# Revit family: Haworth_Riverbend_StraightBench_AP_PRELIMINARY
name_source: partatom
category: Furniture
revit_build: Autodesk Revit 2018 (Build: 20170223_1515(x64)
units: mm (PartAtom-declared; Revit-internal decimal feet)

## family parameters
Always vertical = Yes
Cut with Voids When Loaded = No
OmniClass Number = 23.40.70.14.64.21
OmniClass Title = Systems Furniture
Room Calculation Point = No
Shared = No
Work Plane-Based = No

## types (4) — shared parameters
Actual Depth = 795 mm  [stored 2.60827 ft]
Assembly Code = E2020200
Custom Size = No
Custom Width = No
Depth = 795 mm  [stored 2.60827 ft]
Description = Haworth - Riverbend - Straight Bench
Front Finish = Haworth _ Plastic _ Black
Hardware Finish = Haworth _ Paint _ Plaster
Manufacturer = Haworth
Max. Depth = 850 mm  [stored 2.78871 ft]
Max. Width = 2000 mm  [stored 6.56168 ft]
Min. Depth = 795 mm  [stored 2.60827 ft]
Min. Width = 700 mm  [stored 2.29659 ft]
Model = SERISXNX
Revision Number = 1
Size = Verify Final Dim. w/ Haworth
Trim Finish = Haworth _ Paint _ Plaster
URL = https://www.haworth.com
URL - Product = https://www.haworth.com
Warranty = http://www.haworth.com

## per-type parameters (varying)
| type | Actual Height | Actual Width | High | High Back | Low | Mid Back | No Back | Width |
| 700w x 795d x 720h - Mid Back | 390 mm  [stored 1.27953 ft] | 700 mm  [stored 2.29659 ft] | No | No | Yes | Yes | No | 700 mm  [stored 2.29659 ft] |
| 1400w x 795d x 720h - High Back | 390 mm  [stored 1.27953 ft] | 1400 mm  [stored 4.59318 ft] | No | Yes | Yes | No | No | 1400 mm  [stored 4.59318 ft] |
| 1700w x 795d x 720h - No Back | 390 mm  [stored 1.27953 ft] | 1700 mm  [stored 5.57743 ft] | No | No | Yes | No | Yes | 1700 mm  [stored 5.57743 ft] |
| 2000w x 795d x 720h - High Back | 450 mm  [stored 1.47638 ft] | 2000 mm  [stored 6.56168 ft] | Yes | Yes | No | No | No | 2000 mm  [stored 6.56168 ft] |

note: [stored X ft] marks values corroborated as IEEE doubles in the binary element streams (Revit-internal decimal feet)

## geometry (parser evidence)
native form markers: Sweep x15
no freeform markers — native parametric forms only
